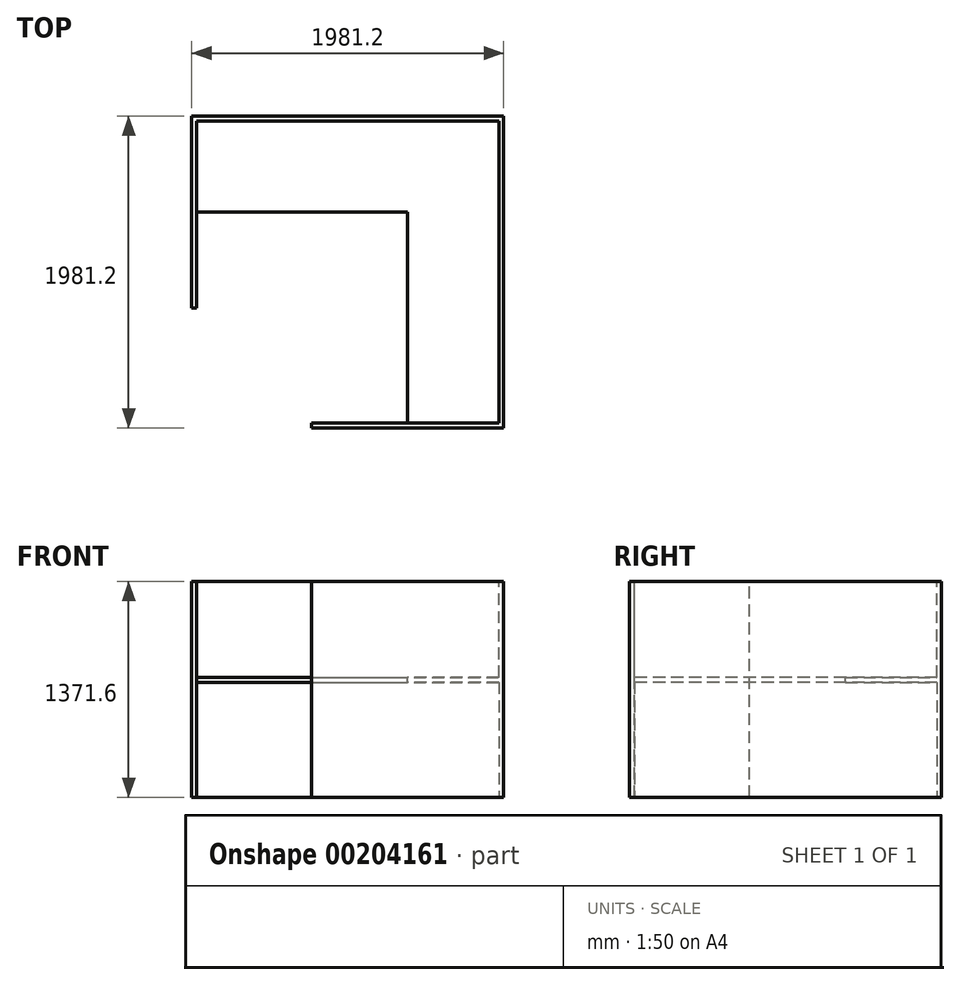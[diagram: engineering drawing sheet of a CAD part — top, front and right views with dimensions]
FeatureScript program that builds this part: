
annotation { "Feature Type Name" : "Feature", "Feature Type Description" : "" }
export const myFeature = defineFeature(function(context is Context, id is Id, definition is map)
    precondition{}
    {
        {
            var Q0;
            Q0=qCreatedBy(makeId("Top.planeOp"),FACE);
            var sketch = newSketch(context, id + "F0", { "sketchPlane" : qUnion([Q0])});
            skLineSegment(sketch, "E0.bottom", {"start": v(0, 0) * mm, "end": v(1981.2, 0) * mm});
            skLineSegment(sketch, "E0.top", {"start": v(0, 1981.2) * mm, "end": v(1981.2, 1981.2) * mm});
            skLineSegment(sketch, "E0.left", {"start": v(0, 0) * mm, "end": v(0, 1981.2) * mm});
            skLineSegment(sketch, "E0.right", {"start": v(1981.2, 0) * mm, "end": v(1981.2, 1981.2) * mm});
            skSolve(sketch);
        }
        {
            var Q0;
            Q0 = qSketchRegion(id + "F0", true);
            extrude(context, id + "F1", {"entities" : qUnion([Q0]), "depth" : 1371.6 * mm});
        }
        {
            var Q0;
            Q0=makeQuery(id+"F1.opExtrude","CAP_FACE",FACE,{"disambiguationData":[OSD([sQuery(id+"F0.wireOp",EDGE,"E0.bottom"),sQuery(id+"F0.wireOp",EDGE,"E0.top"),sQuery(id+"F0.wireOp",EDGE,"E0.left"),sQuery(id+"F0.wireOp",EDGE,"E0.right")])],"isStart":false});
            var sketch = newSketch(context, id + "F2", { "sketchPlane" : qUnion([Q0])});
            skLineSegment(sketch, "E1", {"start": v(1371.6, 1371.6) * mm, "end": v(1371.6, 465.32) * mm});
            skLineSegment(sketch, "E2", {"start": v(30.48, 1371.6) * mm, "end": v(1371.6, 1371.6) * mm});
            skPoint(sketch, "E3.start.orphan", {"position": v(1950.72, 0) * mm});
            skLineSegment(sketch, "E4", {"start": v(1371.6, 465.32) * mm, "end": v(1371.6, 30.48) * mm});
            skLineSegment(sketch, "E5", {"start": v(1371.6, 30.48) * mm, "end": v(762, 30.48) * mm});
            skLineSegment(sketch, "E6", {"start": v(30.48, 1371.6) * mm, "end": v(30.48, 762) * mm});
            skLineSegment(sketch, "E7", {"start": v(30.48, 762) * mm, "end": v(0, 762) * mm});
            skLineSegment(sketch, "E8", {"start": v(0, 762) * mm, "end": v(0, 0) * mm});
            skLineSegment(sketch, "E9", {"start": v(762, 30.48) * mm, "end": v(762, 0) * mm});
            skLineSegment(sketch, "E10", {"start": v(762, 0) * mm, "end": v(0, 0) * mm});
            skSolve(sketch);
        }
        {
            var Q0;
            Q0=makeQuery(id+"F2.imprint","IMPRINT",FACE,{"disambiguationData":[TD([[makeQuery(id+"F2.imprint","IMPRINT",EDGE,{"derivedFrom":sQuery(id+"F2.wireOp",EDGE,"E1")}),-1.0]])]});
            extrude(context, id + "F3", {"entities" : qUnion([Q0]), "operationType" : NewBodyOperationType.REMOVE, "oppositeDirection" : true, "depth" : 1524 * mm});
        }
        {
            var Q0;
            Q0=makeQuery(id+"F1.opExtrude","CAP_FACE",FACE,{"disambiguationData":[OSD([sQuery(id+"F0.wireOp",EDGE,"E0.bottom"),sQuery(id+"F0.wireOp",EDGE,"E0.top"),sQuery(id+"F0.wireOp",EDGE,"E0.left"),sQuery(id+"F0.wireOp",EDGE,"E0.right")])],"isStart":false});
            var sketch = newSketch(context, id + "F4", { "sketchPlane" : qUnion([Q0])});
            skLineSegment(sketch, "E11", {"start": v(30.48, 1371.6) * mm, "end": v(30.48, 1950.72) * mm});
            skLineSegment(sketch, "E12", {"start": v(30.48, 1950.72) * mm, "end": v(1950.72, 1950.72) * mm});
            skLineSegment(sketch, "E13", {"start": v(1950.72, 1950.72) * mm, "end": v(1950.72, 30.48) * mm});
            skLineSegment(sketch, "E14", {"start": v(1950.72, 30.48) * mm, "end": v(1371.6, 30.48) * mm});
            skLineSegment(sketch, "E15", {"start": v(1371.6, 30.48) * mm, "end": v(1371.6, 1371.6) * mm});
            skLineSegment(sketch, "E16", {"start": v(1371.6, 1371.6) * mm, "end": v(30.48, 1371.6) * mm});
            skSolve(sketch);
        }
        {
            var Q0;
            Q0 = qSketchRegion(id + "F4", true);
            extrude(context, id + "F5", {"entities" : qUnion([Q0]), "operationType" : NewBodyOperationType.REMOVE, "oppositeDirection" : true, "depth" : 609.6 * mm});
        }
        {
            var Q0;
            Q0=makeQuery(id+"F1.opExtrude","CAP_FACE",FACE,{"disambiguationData":[OSD([sQuery(id+"F0.wireOp",EDGE,"E0.bottom"),sQuery(id+"F0.wireOp",EDGE,"E0.top"),sQuery(id+"F0.wireOp",EDGE,"E0.left"),sQuery(id+"F0.wireOp",EDGE,"E0.right")])],"isStart":true});
            var sketch = newSketch(context, id + "F6", { "sketchPlane" : qUnion([Q0])});
            skLineSegment(sketch, "E17", {"start": v(30.48, -1371.6) * mm, "end": v(30.48, -1950.72) * mm});
            skLineSegment(sketch, "E18", {"start": v(30.48, -1950.72) * mm, "end": v(1950.72, -1950.72) * mm});
            skLineSegment(sketch, "E19", {"start": v(1950.72, -1950.72) * mm, "end": v(1950.72, -30.48) * mm});
            skLineSegment(sketch, "E20", {"start": v(1950.72, -30.48) * mm, "end": v(1371.6, -30.48) * mm});
            skLineSegment(sketch, "E21", {"start": v(1371.6, -30.48) * mm, "end": v(1371.6, -1371.6) * mm});
            skLineSegment(sketch, "E22", {"start": v(1371.6, -1371.6) * mm, "end": v(30.48, -1371.6) * mm});
            skSolve(sketch);
        }
        {
            var Q0;
            Q0=makeQuery(id+"F6.imprint","IMPRINT",FACE,{"disambiguationData":[TD([[makeQuery(id+"F6.imprint","IMPRINT",EDGE,{"derivedFrom":sQuery(id+"F6.wireOp",EDGE,"E17")}),1.0]])]});
            extrude(context, id + "F7", {"entities" : qUnion([Q0]), "operationType" : NewBodyOperationType.REMOVE, "oppositeDirection" : true, "depth" : 731.52 * mm});
        }
    });
